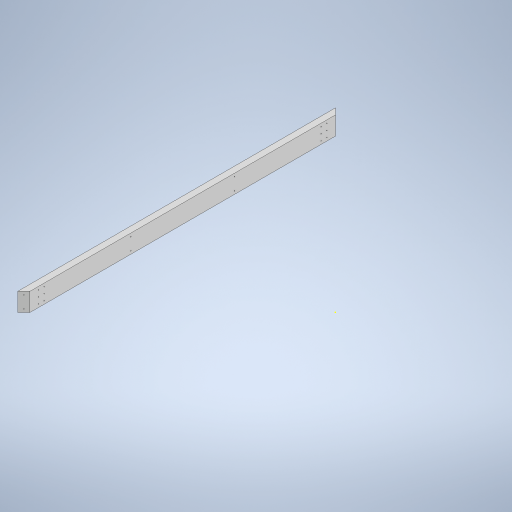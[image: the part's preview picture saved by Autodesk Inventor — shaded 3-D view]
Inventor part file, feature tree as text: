
AUTODESK INVENTOR PART (.ipt)
format: ipt  version: 2023 (Build 270158000, 158)  size: 433,664 bytes
history: native  units: in
note: dims shown in document units (in); Inventor stores cm internally (conversion verified against a paired STEP export)
features: other x9, hole x8, sketch x6, extrude x5, chamfer x2
ambient origin geometry x8: Origin, YZ Plane, XZ Plane, XY Plane, X Axis, Y Axis, Z Axis, Center Point
bodies: Solid1 (feature_tree)
feature tree (30):
  extrude  "Extrusion1"  Depth=54.0in
  sketch  "Sketch2"  dims[d2=1.0in d3=1.0in]
  extrude  "Extrusion2"  Depth=1.0in
  extrude  "Extrusion3"  Depth=16.0in
  other  "Work Axis1"
  other  "Work Axis2"
  other  "Work Axis3"
  other  "Work Point1"
  other  "Work Point2"
  other  "Work Axis4"
  other  "Work Axis5"
  other  "Work Point3"
  other  "Work Point4"
  hole  "Hole1"  [1 undecoded]
  hole  "Hole2"  [1 undecoded]
  hole  "Hole3"  [1 undecoded]
  hole  "Hole4"  [1 undecoded]
  hole  "Hole5"  [1 undecoded]
  hole  "Hole6"  [1 undecoded]
  hole  "Hole7"  [1 undecoded]
  hole  "Hole8"  [1 undecoded]
  extrude  "Extrusion4"  Depth=0.125in
  chamfer  "Chamfer1"  Distance=17.0in
  extrude  "Extrusion5"  Depth=0.125in
  chamfer  "Chamfer2"  Distance=20.0in
  sketch  "Sketch1"  dims[d0=54.0in d1=54.0in]
  sketch  "Sketch3"  dims[d4=8.0in d5=16.0in]
  sketch  "Sketch4"  dims[d6=8.0in d7=16.0in]
  sketch  "Sketch5"  dims[d8=16.0in d9=8.0in]
  sketch  "Sketch6"  dims[d10=16.0in d11=8.0in d12=4.0in d13=4.0in d14=4.0in d15=4.0in d16=17.0in d17=17.0in d18=17.0in d19=17.0in d20=20.0in d21=1.0in d22=1.0in d23=1.0in d24=1.0in d25=45.0deg d26=2.5in d27=45.0deg d28=45.0deg d29=45.0deg d30=1.0in d31=1.0in d32=1.0in d33=1.0in d34=0.25in d35=0.25in d36=0.25in d37=0.25in d38=0.25in d39=0.25in d40=0.25in d41=0.25in d42=3.0in d43=0.0in d44=0.125in d45=0.125in d46=0.707in d47=0.707in d48=0.5in d49=0.5in d50=3.0in d51=0.0in d52=0.125in d53=0.125in d54=0.707in d55=0.707in d56=0.5in d57=0.5in d58=3.0in d59=0.0in d60=1.0in d61=1.0in d62=0.25in d63=0.75in d64=0.375in d65=0.25in d66=0.5635in d67=0.15in d68=0.0in d69=1.0in d70=1.0in d71=0.25in d72=0.75in d73=0.375in d74=0.25in d75=0.5635in d76=0.15in d77=0.0in d78=1.0in d79=1.0in d80=0.25in d81=0.75in d82=0.375in d83=0.25in d84=0.5635in d85=0.15in d86=0.0in d87=1.0in d88=1.0in d89=0.25in d90=0.75in d91=0.375in d92=0.25in d93=0.5635in d94=0.15in d95=0.0in d96=1.0in d97=1.0in d98=0.25in d99=0.75in d100=0.375in d101=0.25in d102=0.5635in d103=0.15in d104=0.0in d105=1.0in d106=1.0in d107=0.25in d108=0.75in d109=0.375in d110=0.25in d111=0.5635in d112=0.15in d113=0.0in d114=1.0in d115=1.0in d116=0.25in d117=0.75in d118=0.375in d119=0.25in d120=0.5635in d121=0.15in d122=0.0in d123=1.0in d124=1.0in d125=0.25in d126=0.75in d127=0.375in d128=0.25in d129=0.5635in d130=0.15in d131=0.0in d132=0.125in d133=0.125in d134=0.5in d135=0.5in d136=0.5in d137=0.5in d138=0.125in d139=0.125in d140=0.5in d141=0.5in d142=0.5in d143=0.5in d144=3.0in d145=0.0in d146=0.125in d147=0.125in d148=45.0deg d149=0.125in d150=0.125in d151=0.125in d152=0.125in d153=0.125in d154=0.125in d155=0.5in d156=0.5in d157=1.5in d158=1.5in d159=0.5in d160=0.5in d161=1.414in d162=1.414in d163=1.414in d164=0.914in d165=0.914in d166=0.914in d167=3.0in d168=0.0in d169=0.125in d170=0.125in d171=45.0deg d172=26.0in]
note: 8 required parameter values undecoded (feature->parameter linkage not recoverable at this tier; creation-order binding heuristic only, values carry confidence <= 0.55)
